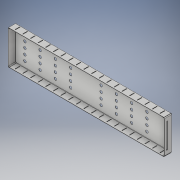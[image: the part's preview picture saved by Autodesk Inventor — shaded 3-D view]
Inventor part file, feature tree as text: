
AUTODESK INVENTOR PART (.ipt)
format: ipt  version: 2018 (Build 220112000, 112)  size: 535,552 bytes
history: native  units: in
note: dims shown in document units (in); Inventor stores cm internally (conversion verified against a paired STEP export)
features: sheet_metal_op x7, sketch x6, other x4, extrude x3, projected_geometry x1
ambient origin geometry x8: Origin, YZ Plane, XZ Plane, XY Plane, X Axis, Y Axis, Z Axis, Center Point
bodies: Body1 (feature_tree)
feature tree (21):
  other  "ImportedSketch"
  sheet_metal_op  "Face3"
  sheet_metal_op  "Flange4"
  sheet_metal_op  "Flange5"
  extrude  "Extrusion1"  Depth=0.25in
  extrude  "Extrusion2"  Depth=0.25in
  extrude  "Extrusion3"  Depth=0.0394in
  sketch  "Sketch6"  dims[d9=0.25in d10=0.25in]
  other  "Plate6"
  sketch  "Sketch10"  dims[d11=0.25in d12=0.25in]
  other  "Plate7"
  sheet_metal_op  "Bend4"
  sheet_metal_op  "Corner4"
  sketch  "Sketch11"  dims[d44=0.0394in d45=0.0394in]
  other  "Plate8"
  sheet_metal_op  "Bend5"
  sheet_metal_op  "Corner5"
  sketch  "Sketch13"  dims[d46=0.0197in]
  sketch  "Sketch14"  dims[d47=0.0787in]
  sketch  "Sketch15"  dims[d48=0.0394in d49=1.0in d50=90.0deg d51=0.0394in d52=0.1575in d53=0.0394in d54=0.0394in d55=0.0394in d56=0.0197in d57=0.0787in d58=0.0394in d59=0.2in d60=90.0deg d61=0.0394in d62=0.1575in d63=0.0394in d64=0.0394in d65=0.35in d66=0.46in d67=1.0in d68=1.5748in d70=2.0in d71=1.9685in d73=0.75in d76=0.0in d77=0.0in d78=0.7874in d80=10.0in d81=0.3937in d83=1.0in d85=0.0787in d86=0.75in d87=0.5in d88=0.625in d89=7.874in d91=1.0in d92=0.3937in d94=1.0in d96=1.0in d97=0.0in d98=0.2in d99=1.0in d100=0.0in]
  projected_geometry  "Projected Loop1"
